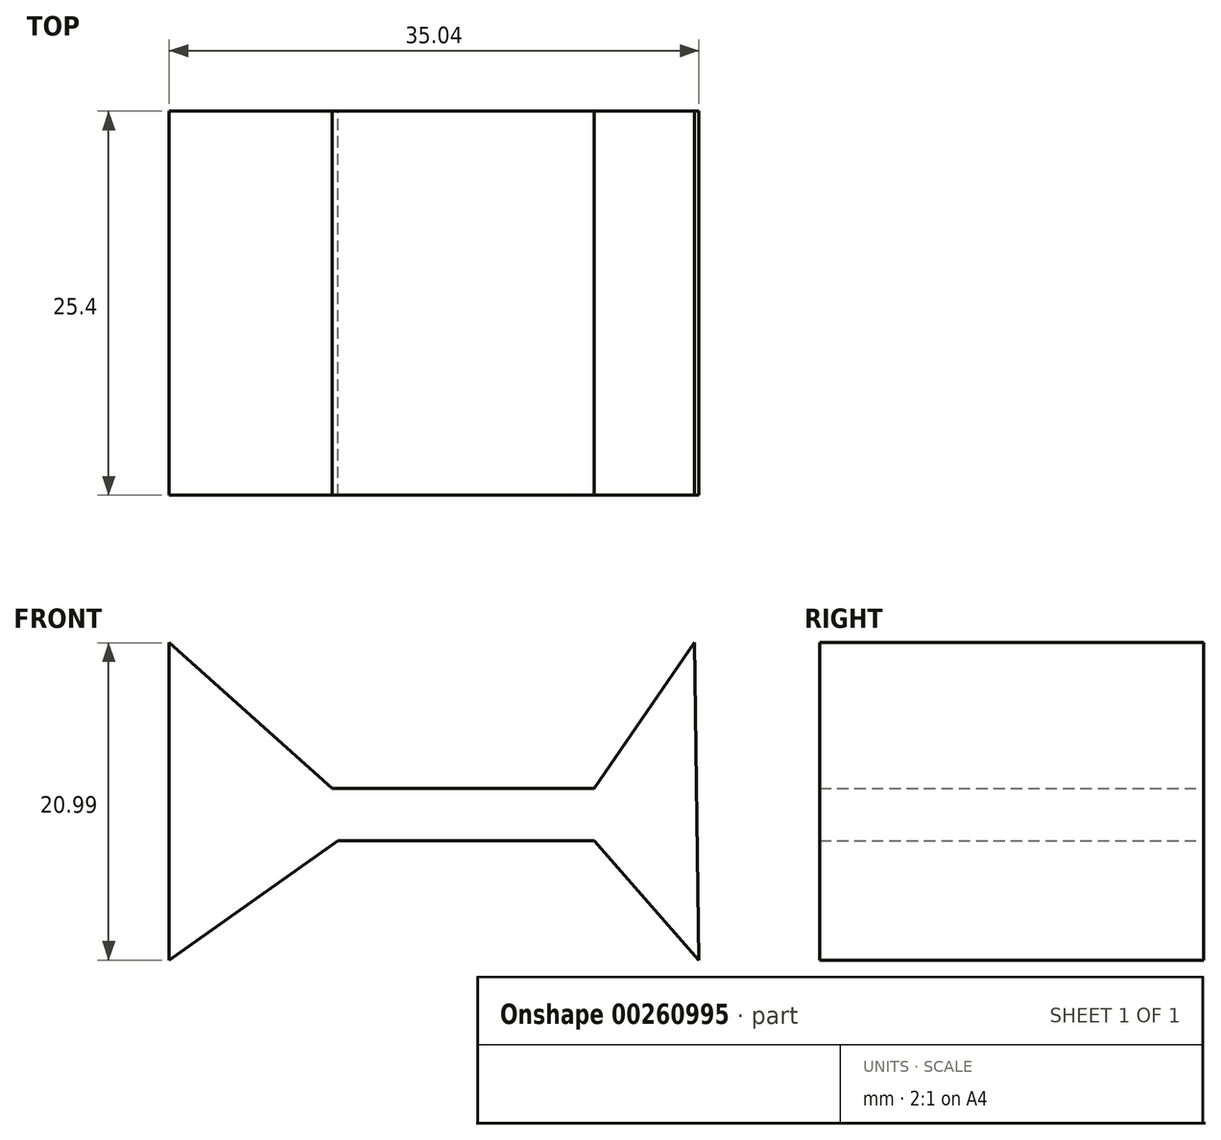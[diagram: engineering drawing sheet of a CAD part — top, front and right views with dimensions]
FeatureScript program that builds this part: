
annotation { "Feature Type Name" : "Feature", "Feature Type Description" : "" }
export const myFeature = defineFeature(function(context is Context, id is Id, definition is map)
    precondition{}
    {
        {
            var Q0;
            Q0=qCreatedBy(makeId("Front.planeOp"),FACE);
            var sketch = newSketch(context, id + "F0", { "sketchPlane" : qUnion([Q0])});
            skLineSegment(sketch, "E0", {"start": v(-21.18, 33.6) * mm, "end": v(-21.18, 12.61) * mm});
            skLineSegment(sketch, "E1", {"start": v(-21.18, 33.6) * mm, "end": v(-10.4, 23.97) * mm});
            skLineSegment(sketch, "E2", {"start": v(-21.18, 12.61) * mm, "end": v(-10.01, 20.5) * mm});
            skLineSegment(sketch, "E3", {"start": v(-10.01, 20.5) * mm, "end": v(6.93, 20.5) * mm});
            skLineSegment(sketch, "E4", {"start": v(6.93, 20.5) * mm, "end": v(13.86, 12.61) * mm});
            skLineSegment(sketch, "E5", {"start": v(13.86, 12.42) * mm, "end": v(28.11, 12.61) * mm});
            skLineSegment(sketch, "E6", {"start": v(13.86, 12.61) * mm, "end": v(13.58, 33.6) * mm});
            skLineSegment(sketch, "E7", {"start": v(-10.4, 23.97) * mm, "end": v(6.93, 23.97) * mm});
            skLineSegment(sketch, "E8", {"start": v(6.93, 23.97) * mm, "end": v(13.58, 33.6) * mm});
            skSolve(sketch);
        }
        {
            var Q0;
            Q0 = qSketchRegion(id + "F0", true);
            extrude(context, id + "F1", {"entities" : qUnion([Q0]), "depth" : 25.4 * mm});
        }
    });
